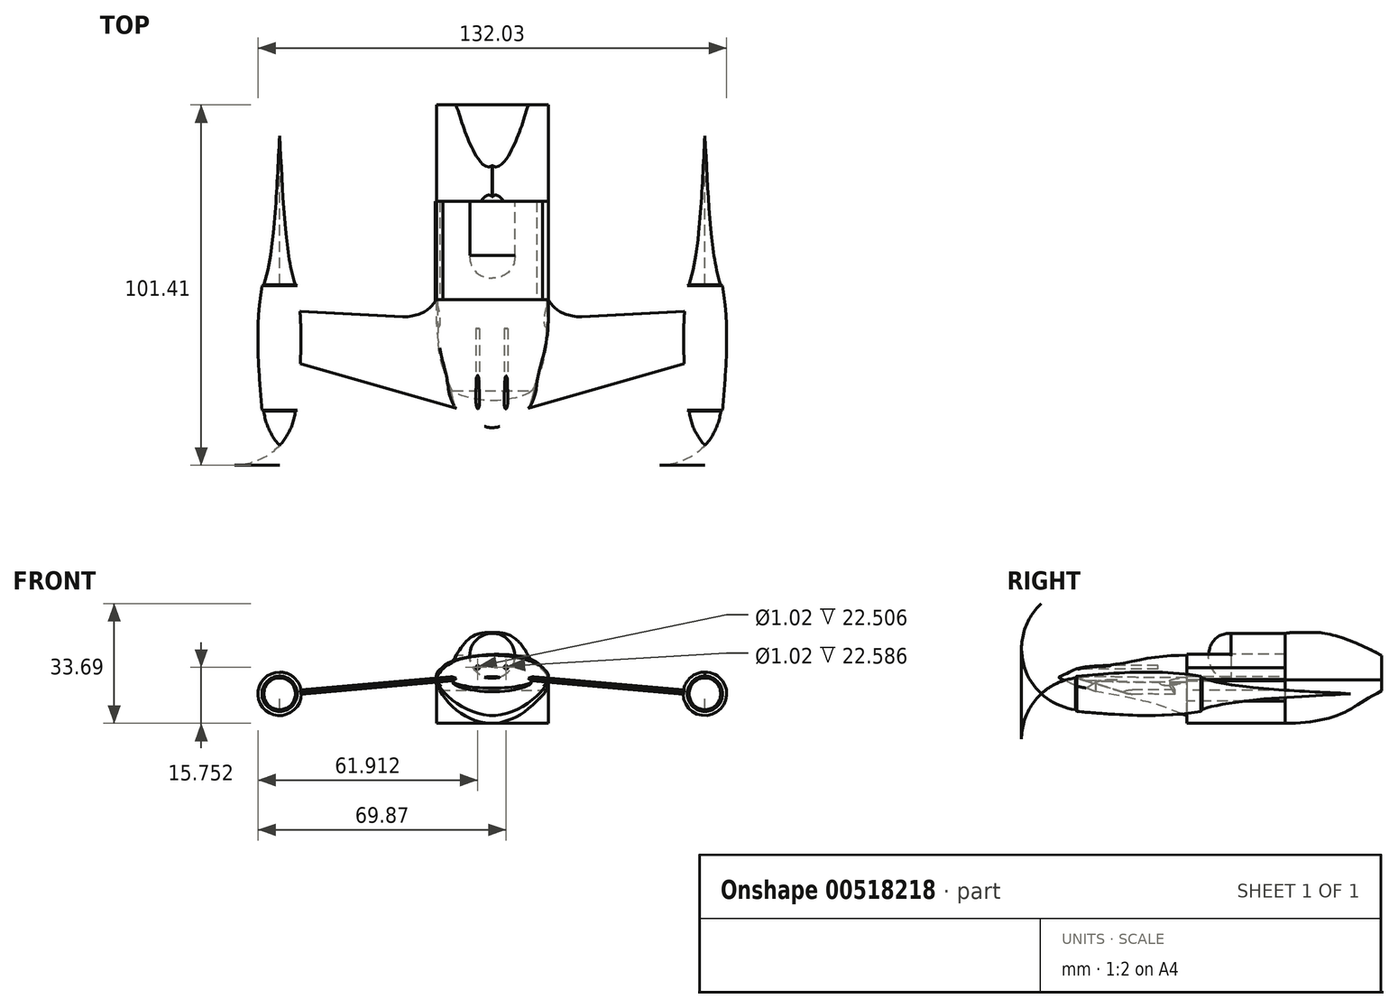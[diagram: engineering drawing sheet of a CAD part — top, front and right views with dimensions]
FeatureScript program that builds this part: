
annotation { "Feature Type Name" : "Feature", "Feature Type Description" : "" }
export const myFeature = defineFeature(function(context is Context, id is Id, definition is map)
    precondition{}
    {
        {
            var Q0;
            Q0=qCreatedBy(makeId("Top.planeOp"),FACE);
            var sketch = newSketch(context, id + "F0", { "sketchPlane" : qUnion([Q0])});
            skLineSegment(sketch, "E0", {"start": v(-12.65, -20.32) * mm, "end": v(-63.92, -5.62) * mm});
            skLineSegment(sketch, "E1", {"start": v(-28.8, 5.88) * mm, "end": v(-63.92, 7.72) * mm});
            skFitSpline(sketch, "E2", {"points": [v(-28.8, 5.88) * mm, v(-18.92, 16.89) * mm], "startDerivative": vector(26.2, 1.25) * mm, "endDerivative": vector(2.67, 12.14) * mm});
            skLineSegment(sketch, "E3", {"start": v(-63.92, 7.72) * mm, "end": v(-63.92, -5.62) * mm});
            skSolve(sketch);
        }
        {
            var Q0;
            Q0=qCreatedBy(makeId("Top.planeOp"),FACE);
            var Q1;
            Q1=sQuery(id+"F0.wireOp",EDGE,"E3");
            cPlane(context, id + "F1", {"entities" : qUnion([Q0, Q1]), "cplaneType" : CPlaneType.LINE_ANGLE, "offset" : 25.4 * mm, "angle" : 185 * degree, "width" : 152.4 * mm, "height" : 152.4 * mm});
        }
        {
            var Q0;
            Q0=qCreatedBy(id+"F1.planeOp",FACE);
            var sketch = newSketch(context, id + "F2", { "sketchPlane" : qUnion([Q0])});
            skLineSegment(sketch, "E4", {"start": v(-63.74, 6.67) * mm, "end": v(-63.74, -6.67) * mm});
            skLineSegment(sketch, "E5", {"start": v(-63.74, 6.67) * mm, "end": v(-28.61, 4.83) * mm});
            skLineSegment(sketch, "E6", {"start": v(-63.74, -6.67) * mm, "end": v(-12.47, -21.37) * mm});
            skFitSpline(sketch, "E7", {"points": [v(-28.61, 4.83) * mm, v(-17.53, 15.9) * mm], "startDerivative": vector(29.82, 1.4) * mm, "endDerivative": vector(2.66, 12.89) * mm});
            skFitSpline(sketch, "E8", {"points": [v(-17.53, 15.9) * mm, v(-12.47, -21.37) * mm], "startDerivative": vector(-1.14, -43.58) * mm, "endDerivative": vector(17.08, -27.32) * mm});
            skSolve(sketch);
        }
        {
            var Q0;
            Q0 = qSketchRegion(id + "F2", true);
            extrude(context, id + "F3", {"entities" : qUnion([Q0]), "endBound" : BoundingType.SYMMETRIC, "depth" : 1.27 * mm, "offsetDistance" : 25.4 * mm});
        }
        {
            var Q0;
            Q0=qCreatedBy(makeId("Right.planeOp"),FACE);
            cPlane(context, id + "F4", {"entities" : qUnion([Q0]), "cplaneType" : CPlaneType.OFFSET, "offset" : 63.75 * mm, "oppositeDirection" : true, "width" : 152.4 * mm, "height" : 152.4 * mm});
        }
        {
            var Q0;
            Q0=qCreatedBy(id+"F4.planeOp",FACE);
            var sketch = newSketch(context, id + "F5", { "sketchPlane" : qUnion([Q0])});
            skArc(sketch, "E9", {"start": v(-31.34, 0) * mm, "mid": v(-26.88, -2.98) * mm, "end": v(-21.72, -4.45) * mm});
            skFitSpline(sketch, "E10", {"points": [v(-21.72, -4.95) * mm, v(13.64, -4.95) * mm], "startDerivative": vector(34.57, -2.86) * mm, "endDerivative": vector(36.11, 6.19) * mm});
            skFitSpline(sketch, "E11", {"points": [v(13.95, -4.43) * mm, v(55.82, 0) * mm], "startDerivative": vector(26.67, 9.84) * mm, "endDerivative": vector(28.85, 1.9) * mm});
            skLineSegment(sketch, "E12", {"start": v(13.95, -4.43) * mm, "end": v(13.64, -4.95) * mm});
            skLineSegment(sketch, "E13", {"start": v(-21.39, -4.98) * mm, "end": v(-21.72, -4.45) * mm});
            skLineSegment(sketch, "E14", {"start": v(55.82, 0) * mm, "end": v(-31.34, 0) * mm});
            skSolve(sketch);
        }
        {
            var Q0;
            Q0 = qSketchRegion(id + "F5", true);
            var Q1;
            Q1=sQuery(id+"F5.wireOp",EDGE,"E14");
            revolve(context, id + "F6", {"operationType" : NewBodyOperationType.ADD, "entities" : qUnion([Q0]), "axis" : qUnion([Q1]), "revolveType" : RevolveType.FULL});
        }
        {
            var Q0;
            Q0=qCreatedBy(makeId("Front.planeOp"),FACE);
            cPlane(context, id + "F7", {"entities" : qUnion([Q0]), "cplaneType" : CPlaneType.OFFSET, "offset" : 21.59 * mm, "width" : 152.4 * mm, "height" : 152.4 * mm});
        }
        {
            var Q0;
            Q0=qCreatedBy(makeId("Front.planeOp"),FACE);
            cPlane(context, id + "F8", {"entities" : qUnion([Q0]), "cplaneType" : CPlaneType.OFFSET, "offset" : 6.35 * mm, "width" : 152.4 * mm, "height" : 152.4 * mm});
        }
        {
            var Q0;
            Q0=qCreatedBy(id+"F7.planeOp",FACE);
            var sketch = newSketch(context, id + "F9", { "sketchPlane" : qUnion([Q0])});
            skEllipse(sketch, "E15", {"center": v(-3.86, 4.62) * mm, "majorRadius": 9.54 * mm, "minorRadius": 2.32 * mm, "majorAxis": v(-1, 0)});
            skSolve(sketch);
        }
        {
            var Q0;
            Q0=qCreatedBy(id+"F8.planeOp",FACE);
            var sketch = newSketch(context, id + "F10", { "sketchPlane" : qUnion([Q0])});
            skPoint(sketch, "E16.0", {"position": v(-3.86, 4.62) * mm});
            skEllipse(sketch, "E17", {"center": v(-3.86, 4.62) * mm, "majorRadius": 14.29 * mm, "minorRadius": 4.37 * mm, "majorAxis": v(-1, 0)});
            skSolve(sketch);
        }
        {
            var Q0;
            Q0=qCreatedBy(makeId("Front.planeOp"),FACE);
            var sketch = newSketch(context, id + "F11", { "sketchPlane" : qUnion([Q0])});
            skPoint(sketch, "E18.0", {"position": v(-3.86, 4.62) * mm});
            skEllipse(sketch, "E19", {"center": v(-3.86, 4.62) * mm, "majorRadius": 15.52 * mm, "minorRadius": 5.58 * mm, "majorAxis": v(-1, 0)});
            skSolve(sketch);
        }
        {
            var Q0;
            Q0=qCreatedBy(makeId("Front.planeOp"),FACE);
            cPlane(context, id + "F12", {"entities" : qUnion([Q0]), "cplaneType" : CPlaneType.OFFSET, "offset" : 15.75 * mm, "oppositeDirection" : true, "width" : 152.4 * mm, "height" : 152.4 * mm});
        }
        {
            var Q0;
            Q0=qCreatedBy(id+"F12.planeOp",FACE);
            var sketch = newSketch(context, id + "F13", { "sketchPlane" : qUnion([Q0])});
            skPoint(sketch, "E20.0", {"position": v(-3.86, 4.62) * mm});
            skEllipse(sketch, "E21", {"center": v(-3.86, 4.62) * mm, "majorRadius": 15.24 * mm, "minorRadius": 6.16 * mm, "majorAxis": v(-1, 0)});
            skSolve(sketch);
        }
        {
            var Q0;
            Q0=qCreatedBy(id+"F7.planeOp",FACE);
            cPlane(context, id + "F14", {"entities" : qUnion([Q0]), "cplaneType" : CPlaneType.OFFSET, "offset" : 5.08 * mm, "width" : 152.4 * mm, "height" : 152.4 * mm});
        }
        {
            var Q0;
            Q0=qCreatedBy(id+"F14.planeOp",FACE);
            var sketch = newSketch(context, id + "F15", { "sketchPlane" : qUnion([Q0])});
            skPoint(sketch, "E22.0", {"position": v(-3.86, 4.62) * mm});
            skEllipse(sketch, "E23", {"center": v(-3.86, 4.62) * mm, "majorRadius": 0.64 * mm, "minorRadius": 0.04 * mm, "majorAxis": v(1, 0)});
            skSolve(sketch);
        }
        {
            var Q0;
            Q0=qCreatedBy(id+"F14.planeOp",FACE);
            cPlane(context, id + "F16", {"entities" : qUnion([Q0]), "cplaneType" : CPlaneType.OFFSET, "offset" : 2.8 * mm, "oppositeDirection" : true, "width" : 152.4 * mm, "height" : 152.4 * mm});
        }
        {
            var Q0;
            Q0=qCreatedBy(id+"F16.planeOp",FACE);
            var sketch = newSketch(context, id + "F17", { "sketchPlane" : qUnion([Q0])});
            skPoint(sketch, "E24.0", {"position": v(-3.86, 4.62) * mm});
            skEllipse(sketch, "E25", {"center": v(-3.86, 4.62) * mm, "majorRadius": 6.39 * mm, "minorRadius": 1.25 * mm, "majorAxis": v(-1, 0)});
            skSolve(sketch);
        }
        {
            var Q0;
            Q0=qCreatedBy(id+"F8.planeOp",FACE);
            cPlane(context, id + "F18", {"entities" : qUnion([Q0]), "cplaneType" : CPlaneType.OFFSET, "offset" : 6.6 * mm, "width" : 152.4 * mm, "height" : 152.4 * mm});
        }
        {
            var Q0;
            Q0=qCreatedBy(id+"F18.planeOp",FACE);
            var sketch = newSketch(context, id + "F19", { "sketchPlane" : qUnion([Q0])});
            skPoint(sketch, "E26.0", {"position": v(-3.86, 4.62) * mm});
            skEllipse(sketch, "E27", {"center": v(-3.86, 4.62) * mm, "majorRadius": 12.73 * mm, "minorRadius": 3.38 * mm, "majorAxis": v(-1, 0)});
            skSolve(sketch);
        }
        {
            var Q1;
            Q1=makeQuery(id+"F13.imprint","IMPRINT",FACE,{"disambiguationData":[TD([[makeQuery(id+"F13.imprint","IMPRINT",EDGE,{"derivedFrom":sQuery(id+"F13.wireOp",EDGE,"E21")}),1.0]])]});
            var Q2;
            Q2=makeQuery(id+"F11.imprint","IMPRINT",FACE,{"disambiguationData":[TD([[makeQuery(id+"F11.imprint","IMPRINT",EDGE,{"derivedFrom":sQuery(id+"F11.wireOp",EDGE,"E19")}),1.0]])]});
            var Q3;
            Q3=makeQuery(id+"F10.imprint","IMPRINT",FACE,{"disambiguationData":[TD([[makeQuery(id+"F10.imprint","IMPRINT",EDGE,{"derivedFrom":sQuery(id+"F10.wireOp",EDGE,"E17")}),1.0]])]});
            var Q4;
            Q4=makeQuery(id+"F19.imprint","IMPRINT",FACE,{"disambiguationData":[TD([[makeQuery(id+"F19.imprint","IMPRINT",EDGE,{"derivedFrom":sQuery(id+"F19.wireOp",EDGE,"E27")}),1.0]])]});
            var Q5;
            Q5=makeQuery(id+"F9.imprint","IMPRINT",FACE,{"disambiguationData":[TD([[makeQuery(id+"F9.imprint","IMPRINT",EDGE,{"derivedFrom":sQuery(id+"F9.wireOp",EDGE,"E15")}),1.0]])]});
            var Q6;
            Q6=makeQuery(id+"F17.imprint","IMPRINT",FACE,{"disambiguationData":[TD([[makeQuery(id+"F17.imprint","IMPRINT",EDGE,{"derivedFrom":sQuery(id+"F17.wireOp",EDGE,"E25")}),1.0]])]});
            var Q7;
            Q7=makeQuery(id+"F15.imprint","IMPRINT",FACE,{"disambiguationData":[TD([[makeQuery(id+"F15.imprint","IMPRINT",EDGE,{"derivedFrom":sQuery(id+"F15.wireOp",EDGE,"E23")}),1.0]])]});
            loft(context, id + "F20", {"operationType" : NewBodyOperationType.ADD, "sheetProfilesArray" : [{ "sheetProfileEntities" : qUnion([Q1]) }, { "sheetProfileEntities" : qUnion([Q2]) }, { "sheetProfileEntities" : qUnion([Q3]) }, { "sheetProfileEntities" : qUnion([Q4]) }, { "sheetProfileEntities" : qUnion([Q5]) }, { "sheetProfileEntities" : qUnion([Q6]) }, { "sheetProfileEntities" : qUnion([Q7]) }]});
        }
        {
            var Q0;
            Q0=qCreatedBy(makeId("Top.planeOp"),FACE);
            var sketch = newSketch(context, id + "F21", { "sketchPlane" : qUnion([Q0])});
            skArc(sketch, "E28", {"start": v(-6.4, -25.84) * mm, "mid": v(-3.86, -26.34) * mm, "end": v(-1.32, -25.84) * mm});
            skFitSpline(sketch, "E29.0", {"points": [v(-4.5, -26.67) * mm, v(-4.07, -26.67) * mm, v(-3.64, -26.67) * mm, v(-3.22, -26.67) * mm]});
            skLineSegment(sketch, "E30", {"start": v(-6.4, -25.84) * mm, "end": v(-3.91, -27.54) * mm});
            skLineSegment(sketch, "E31", {"start": v(-3.91, -27.54) * mm, "end": v(-1.32, -25.84) * mm});
            skSolve(sketch);
        }
        {
            var Q0;
            Q0 = qSketchRegion(id + "F21", true);
            extrude(context, id + "F22", {"entities" : qUnion([Q0]), "operationType" : NewBodyOperationType.REMOVE, "endBound" : BoundingType.THROUGH_ALL, "depth" : 25.4 * mm, "offsetDistance" : 25.4 * mm});
        }
        {
            var Q0;
            Q0=qCreatedBy(makeId("Right.planeOp"),FACE);
            cPlane(context, id + "F23", {"entities" : qUnion([Q0]), "cplaneType" : CPlaneType.OFFSET, "offset" : 3.86 * mm, "oppositeDirection" : true, "width" : 152.4 * mm, "height" : 152.4 * mm});
        }
        {
            var Q0;
            Q0=makeQuery(id+"F3.opExtrude","SWEPT_BODY",BODY,{"disambiguationData":[OSD([sQuery(id+"F2.wireOp",EDGE,"E4"),sQuery(id+"F2.wireOp",EDGE,"E5"),sQuery(id+"F2.wireOp",EDGE,"E6"),sQuery(id+"F2.wireOp",EDGE,"E7"),sQuery(id+"F2.wireOp",EDGE,"E8")])]});
            var Q1;
            Q1=qCreatedBy(id+"F23.planeOp",FACE);
            mirror(context, id + "F24", {"operationType" : NewBodyOperationType.ADD, "entities" : qUnion([Q0]), "mirrorPlane" : qUnion([Q1])});
        }
        {
            var Q0;
            Q0=qCreatedBy(id+"F16.planeOp",FACE);
            var sketch = newSketch(context, id + "F25", { "sketchPlane" : qUnion([Q0])});
            skCircle(sketch, "E32", {"center": v(0, 7.44) * mm, "radius": 0.5 * mm});
            skCircle(sketch, "E33", {"center": v(-7.96, 7.44) * mm, "radius": 0.5 * mm});
            skSolve(sketch);
        }
        {
            var Q0;
            Q0 = qSketchRegion(id + "F25", true);
            extrude(context, id + "F26", {"entities" : qUnion([Q0]), "operationType" : NewBodyOperationType.REMOVE, "oppositeDirection" : true, "depth" : 25.4 * mm, "offsetDistance" : 25.4 * mm});
        }
        {
            var Q0;
            Q0=makeQuery(id+"F3.opExtrude","CAP_EDGE",EDGE,{"disambiguationData":[OSD([sQuery(id+"F2.wireOp",EDGE,"E6")])],"isStart":false});
            var Q1;
            Q1=makeQuery(id+"F3.opExtrude","CAP_EDGE",EDGE,{"disambiguationData":[OSD([sQuery(id+"F2.wireOp",EDGE,"E6")])],"isStart":true});
            var Q2;
            Q2=makeQuery(id+"F24.opPattern","COPY",EDGE,{"derivedFrom":makeQuery(id+"F3.opExtrude","CAP_EDGE",EDGE,{"disambiguationData":[OSD([sQuery(id+"F2.wireOp",EDGE,"E6")])],"isStart":false}),"instanceName":"1"});
            var Q3;
            Q3=makeQuery(id+"F24.opPattern","COPY",EDGE,{"derivedFrom":makeQuery(id+"F3.opExtrude","CAP_EDGE",EDGE,{"disambiguationData":[OSD([sQuery(id+"F2.wireOp",EDGE,"E6")])],"isStart":true}),"instanceName":"1"});
            chamfer(context, id + "F27", {"entities" : qUnion([Q0, Q1, Q2, Q3]), "width" : 0.76 * mm, "tangentPropagation" : true});
        }
        {
            var Q0;
            Q0=makeQuery(id+"F13.imprint","IMPRINT",FACE,{"disambiguationData":[TD([[makeQuery(id+"F13.imprint","IMPRINT",EDGE,{"derivedFrom":sQuery(id+"F13.wireOp",EDGE,"E21")}),1.0]])]});
            cPlane(context, id + "F28", {"entities" : qUnion([Q0]), "cplaneType" : CPlaneType.OFFSET, "offset" : 6.35 * mm, "oppositeDirection" : true, "width" : 152.4 * mm, "height" : 152.4 * mm});
        }
        {
            var Q0;
            Q0=qCreatedBy(id+"F28.planeOp",FACE);
            cPlane(context, id + "F29", {"entities" : qUnion([Q0]), "cplaneType" : CPlaneType.OFFSET, "offset" : 6.35 * mm, "oppositeDirection" : true, "width" : 152.4 * mm, "height" : 152.4 * mm});
        }
        {
            var Q0;
            Q0=qCreatedBy(id+"F29.planeOp",FACE);
            cPlane(context, id + "F30", {"entities" : qUnion([Q0]), "cplaneType" : CPlaneType.OFFSET, "offset" : 6.35 * mm, "oppositeDirection" : true, "width" : 152.4 * mm, "height" : 152.4 * mm});
        }
        {
            var Q0;
            Q0=qCreatedBy(id+"F30.planeOp",FACE);
            cPlane(context, id + "F31", {"entities" : qUnion([Q0]), "cplaneType" : CPlaneType.OFFSET, "offset" : 6.35 * mm, "oppositeDirection" : true, "width" : 152.4 * mm, "height" : 152.4 * mm});
        }
        {
            var Q0;
            Q0=qCreatedBy(id+"F31.planeOp",FACE);
            cPlane(context, id + "F32", {"entities" : qUnion([Q0]), "cplaneType" : CPlaneType.OFFSET, "offset" : 6.35 * mm, "oppositeDirection" : true, "width" : 152.4 * mm, "height" : 152.4 * mm});
        }
        {
            var Q0;
            Q0=qCreatedBy(id+"F32.planeOp",FACE);
            cPlane(context, id + "F33", {"entities" : qUnion([Q0]), "cplaneType" : CPlaneType.OFFSET, "offset" : 6.35 * mm, "oppositeDirection" : true, "width" : 152.4 * mm, "height" : 152.4 * mm});
        }
        {
            var Q0;
            Q0=qCreatedBy(id+"F33.planeOp",FACE);
            cPlane(context, id + "F34", {"entities" : qUnion([Q0]), "cplaneType" : CPlaneType.OFFSET, "offset" : 6.35 * mm, "oppositeDirection" : true, "width" : 152.4 * mm, "height" : 152.4 * mm});
        }
        {
            var Q0;
            Q0=qCreatedBy(id+"F34.planeOp",FACE);
            cPlane(context, id + "F35", {"entities" : qUnion([Q0]), "cplaneType" : CPlaneType.OFFSET, "offset" : 6.35 * mm, "oppositeDirection" : true, "width" : 152.4 * mm, "height" : 152.4 * mm});
        }
        {
            var Q0;
            Q0=qCreatedBy(id+"F35.planeOp",FACE);
            cPlane(context, id + "F36", {"entities" : qUnion([Q0]), "cplaneType" : CPlaneType.OFFSET, "offset" : 6.35 * mm, "oppositeDirection" : true, "width" : 152.4 * mm, "height" : 152.4 * mm});
        }
        {
            var Q0;
            Q0=qCreatedBy(id+"F36.planeOp",FACE);
            cPlane(context, id + "F37", {"entities" : qUnion([Q0]), "cplaneType" : CPlaneType.OFFSET, "offset" : 6.35 * mm, "oppositeDirection" : true, "width" : 152.4 * mm, "height" : 152.4 * mm});
        }
        {
            var Q0;
            Q0=qCreatedBy(id+"F37.planeOp",FACE);
            cPlane(context, id + "F38", {"entities" : qUnion([Q0]), "cplaneType" : CPlaneType.OFFSET, "offset" : 6.35 * mm, "oppositeDirection" : true, "width" : 152.4 * mm, "height" : 152.4 * mm});
        }
        {
            var Q0;
            Q0=qCreatedBy(id+"F38.planeOp",FACE);
            cPlane(context, id + "F39", {"entities" : qUnion([Q0]), "cplaneType" : CPlaneType.OFFSET, "offset" : 6.35 * mm, "oppositeDirection" : true, "width" : 152.4 * mm, "height" : 152.4 * mm});
        }
        {
            var Q0;
            Q0=qCreatedBy(id+"F39.planeOp",FACE);
            cPlane(context, id + "F40", {"entities" : qUnion([Q0]), "cplaneType" : CPlaneType.OFFSET, "offset" : 6.35 * mm, "oppositeDirection" : true, "width" : 152.4 * mm, "height" : 152.4 * mm});
        }
        {
            var Q0;
            Q0=qCreatedBy(id+"F40.planeOp",FACE);
            cPlane(context, id + "F41", {"entities" : qUnion([Q0]), "cplaneType" : CPlaneType.OFFSET, "offset" : 6.35 * mm, "oppositeDirection" : true, "width" : 152.4 * mm, "height" : 152.4 * mm});
        }
        {
            var Q0;
            {var subQ0=sQuery(id+"F2.wireOp",EDGE,"E7");var subQ1=sQuery(id+"F2.wireOp",EDGE,"E6");var subQ2=sQuery(id+"F2.wireOp",EDGE,"E5");Q0=makeQuery(id+"F27.opChamfer","BLEND_EDGE",EDGE,{"blendedFrom":[makeQuery(id+"F24.opPattern","COPY",EDGE,{"derivedFrom":makeQuery(id+"F3.opExtrude","CAP_EDGE",EDGE,{"disambiguationData":[OSD([subQ1])],"isStart":false}),"instanceName":"1"}),makeQuery(id+"F24.opPattern","COPY",FACE,{"derivedFrom":makeQuery(id+"F20.boolean.opBoolean","SPLIT",FACE,{"disambiguationData":[TD([makeQuery(id+"F3.opExtrude","SWEPT_FACE",FACE,{"disambiguationData":[OSD([subQ2])]})])],"derivedFrom":makeQuery(id+"F3.opExtrude","CAP_FACE",FACE,{"disambiguationData":[OSD([sQuery(id+"F2.wireOp",EDGE,"E4"),subQ2,subQ1,subQ0,sQuery(id+"F2.wireOp",EDGE,"E8")])],"isStart":false})}),"instanceName":"1"})],"blendedInto":[makeQuery(id+"F24.opPattern","COPY",FACE,{"derivedFrom":makeQuery(id+"F20.boolean.opBoolean","SPLIT",FACE,{"disambiguationData":[TD([makeQuery(id+"F3.opExtrude","SWEPT_FACE",FACE,{"disambiguationData":[OSD([subQ2])]})])],"derivedFrom":makeQuery(id+"F3.opExtrude","CAP_FACE",FACE,{"disambiguationData":[OSD([sQuery(id+"F2.wireOp",EDGE,"E4"),subQ2,subQ1,subQ0,sQuery(id+"F2.wireOp",EDGE,"E8")])],"isStart":false})}),"instanceName":"1"})]});}
            var Q1;
            {var subQ0=sQuery(id+"F2.wireOp",EDGE,"E8");var subQ1=sQuery(id+"F2.wireOp",EDGE,"E7");var subQ2=sQuery(id+"F2.wireOp",EDGE,"E6");var subQ3=sQuery(id+"F2.wireOp",EDGE,"E5");Q1=makeQuery(id+"F27.opChamfer","BLEND_EDGE",EDGE,{"blendedFrom":[makeQuery(id+"F24.opPattern","COPY",EDGE,{"derivedFrom":makeQuery(id+"F3.opExtrude","CAP_EDGE",EDGE,{"disambiguationData":[OSD([subQ2])],"isStart":true}),"instanceName":"1"}),makeQuery(id+"F24.opPattern","COPY",FACE,{"derivedFrom":makeQuery(id+"F20.boolean.opBoolean","SPLIT",FACE,{"disambiguationData":[TD([makeQuery(id+"F3.opExtrude","SWEPT_FACE",FACE,{"disambiguationData":[OSD([subQ3])]})])],"derivedFrom":makeQuery(id+"F3.opExtrude","CAP_FACE",FACE,{"disambiguationData":[OSD([sQuery(id+"F2.wireOp",EDGE,"E4"),subQ3,subQ2,subQ1,subQ0])],"isStart":true})}),"instanceName":"1"})],"blendedInto":[makeQuery(id+"F24.opPattern","COPY",FACE,{"derivedFrom":makeQuery(id+"F20.boolean.opBoolean","SPLIT",FACE,{"disambiguationData":[TD([makeQuery(id+"F3.opExtrude","SWEPT_FACE",FACE,{"disambiguationData":[OSD([subQ3])]})])],"derivedFrom":makeQuery(id+"F3.opExtrude","CAP_FACE",FACE,{"disambiguationData":[OSD([sQuery(id+"F2.wireOp",EDGE,"E4"),subQ3,subQ2,subQ1,subQ0])],"isStart":true})}),"instanceName":"1"})]});}
            var Q2;
            {var subQ0=sQuery(id+"F2.wireOp",EDGE,"E7");var subQ1=sQuery(id+"F2.wireOp",EDGE,"E6");var subQ2=sQuery(id+"F2.wireOp",EDGE,"E5");Q2=makeQuery(id+"F27.opChamfer","BLEND_EDGE",EDGE,{"blendedFrom":[makeQuery(id+"F3.opExtrude","CAP_EDGE",EDGE,{"disambiguationData":[OSD([subQ1])],"isStart":false}),makeQuery(id+"F20.boolean.opBoolean","SPLIT",FACE,{"disambiguationData":[TD([makeQuery(id+"F3.opExtrude","SWEPT_FACE",FACE,{"disambiguationData":[OSD([subQ2])]})])],"derivedFrom":makeQuery(id+"F3.opExtrude","CAP_FACE",FACE,{"disambiguationData":[OSD([sQuery(id+"F2.wireOp",EDGE,"E4"),subQ2,subQ1,subQ0,sQuery(id+"F2.wireOp",EDGE,"E8")])],"isStart":false})})],"blendedInto":[makeQuery(id+"F20.boolean.opBoolean","SPLIT",FACE,{"disambiguationData":[TD([makeQuery(id+"F3.opExtrude","SWEPT_FACE",FACE,{"disambiguationData":[OSD([subQ2])]})])],"derivedFrom":makeQuery(id+"F3.opExtrude","CAP_FACE",FACE,{"disambiguationData":[OSD([sQuery(id+"F2.wireOp",EDGE,"E4"),subQ2,subQ1,subQ0,sQuery(id+"F2.wireOp",EDGE,"E8")])],"isStart":false})})]});}
            var Q3;
            {var subQ0=sQuery(id+"F2.wireOp",EDGE,"E8");var subQ1=sQuery(id+"F2.wireOp",EDGE,"E7");var subQ2=sQuery(id+"F2.wireOp",EDGE,"E6");var subQ3=sQuery(id+"F2.wireOp",EDGE,"E5");Q3=makeQuery(id+"F27.opChamfer","BLEND_EDGE",EDGE,{"blendedFrom":[makeQuery(id+"F3.opExtrude","CAP_EDGE",EDGE,{"disambiguationData":[OSD([subQ2])],"isStart":true}),makeQuery(id+"F20.boolean.opBoolean","SPLIT",FACE,{"disambiguationData":[TD([makeQuery(id+"F3.opExtrude","SWEPT_FACE",FACE,{"disambiguationData":[OSD([subQ3])]})])],"derivedFrom":makeQuery(id+"F3.opExtrude","CAP_FACE",FACE,{"disambiguationData":[OSD([sQuery(id+"F2.wireOp",EDGE,"E4"),subQ3,subQ2,subQ1,subQ0])],"isStart":true})})],"blendedInto":[makeQuery(id+"F20.boolean.opBoolean","SPLIT",FACE,{"disambiguationData":[TD([makeQuery(id+"F3.opExtrude","SWEPT_FACE",FACE,{"disambiguationData":[OSD([subQ3])]})])],"derivedFrom":makeQuery(id+"F3.opExtrude","CAP_FACE",FACE,{"disambiguationData":[OSD([sQuery(id+"F2.wireOp",EDGE,"E4"),subQ3,subQ2,subQ1,subQ0])],"isStart":true})})]});}
            fillet(context, id + "F42", {"entities" : qUnion([Q0, Q1, Q2, Q3]), "radius" : 5.08 * mm, "tangentPropagation" : true, "allowEdgeOverflow" : false});
        }
        {
            var Q0;
            Q0=qCreatedBy(id+"F28.planeOp",FACE);
            cPlane(context, id + "F43", {"entities" : qUnion([Q0]), "cplaneType" : CPlaneType.OFFSET, "offset" : 6.35 * mm, "width" : 152.4 * mm, "height" : 152.4 * mm});
        }
        {
            var Q0;
            Q0=qCreatedBy(id+"F43.planeOp",FACE);
            cPlane(context, id + "F44", {"entities" : qUnion([Q0]), "cplaneType" : CPlaneType.OFFSET, "offset" : 6.35 * mm, "width" : 152.4 * mm, "height" : 152.4 * mm});
        }
        {
            var Q0;
            Q0=qCreatedBy(id+"F44.planeOp",FACE);
            cPlane(context, id + "F45", {"entities" : qUnion([Q0]), "cplaneType" : CPlaneType.OFFSET, "offset" : 6.35 * mm, "width" : 152.4 * mm, "height" : 152.4 * mm});
        }
        {
            var Q0;
            Q0=qCreatedBy(id+"F45.planeOp",FACE);
            cPlane(context, id + "F46", {"entities" : qUnion([Q0]), "cplaneType" : CPlaneType.OFFSET, "offset" : 6.35 * mm, "width" : 152.4 * mm, "height" : 152.4 * mm});
        }
        {
            var Q0;
            Q0=qCreatedBy(id+"F46.planeOp",FACE);
            var sketch = newSketch(context, id + "F47", { "sketchPlane" : qUnion([Q0])});
            skFitSpline(sketch, "E34", {"points": [v(-19.58, 3.93) * mm, v(-14.39, 0) * mm, v(-3.8, -1.84) * mm, v(6.67, 0) * mm, v(11.87, 3.88) * mm], "startDerivative": vector(14.64, -24.75) * mm, "endDerivative": vector(15.16, 24.08) * mm});
            skLineSegment(sketch, "E35", {"start": v(-19.58, 3.93) * mm, "end": v(11.87, 3.88) * mm});
            skSolve(sketch);
        }
        {
            var Q0;
            Q0=qCreatedBy(id+"F45.planeOp",FACE);
            var sketch = newSketch(context, id + "F48", { "sketchPlane" : qUnion([Q0])});
            skLineSegment(sketch, "E36.0", {"start": v(-19.58, 3.93) * mm, "end": v(11.87, 3.88) * mm});
            skFitSpline(sketch, "E37", {"points": [v(-19.58, 3.93) * mm, v(-16.04, 0) * mm, v(-3.8, -3.61) * mm, v(8.33, 0) * mm, v(11.87, 3.88) * mm], "startDerivative": vector(14.16, -20.4) * mm, "endDerivative": vector(15.04, 19.9) * mm});
            skPoint(sketch, "E38.0", {"position": v(-14.39, 0) * mm});
            skPoint(sketch, "E39.0", {"position": v(6.67, 0) * mm});
            skSolve(sketch);
        }
        {
            var Q0;
            Q0=qCreatedBy(id+"F44.planeOp",FACE);
            var sketch = newSketch(context, id + "F49", { "sketchPlane" : qUnion([Q0])});
            skLineSegment(sketch, "E40.0", {"start": v(-19.58, 3.93) * mm, "end": v(11.87, 3.88) * mm});
            skPoint(sketch, "E41.0", {"position": v(-3.8, -3.61) * mm});
            skPoint(sketch, "E42.0", {"position": v(8.33, 0) * mm});
            skPoint(sketch, "E43.0", {"position": v(-16.04, 0) * mm});
            skFitSpline(sketch, "E44", {"points": [v(-19.58, 3.93) * mm, v(-17.05, 0) * mm, v(-3.8, -6.08) * mm, v(9.34, 0) * mm, v(11.87, 3.88) * mm], "startDerivative": vector(9, -20.7) * mm, "endDerivative": vector(8.66, 20.62) * mm});
            skSolve(sketch);
        }
        {
            var Q0;
            Q0=qCreatedBy(id+"F43.planeOp",FACE);
            var sketch = newSketch(context, id + "F50", { "sketchPlane" : qUnion([Q0])});
            skLineSegment(sketch, "E45.0", {"start": v(-19.58, 3.93) * mm, "end": v(11.87, 3.88) * mm});
            skPoint(sketch, "E46.0", {"position": v(-3.8, -6.08) * mm});
            skFitSpline(sketch, "E47", {"points": [v(-19.58, 3.93) * mm, v(-17.82, 0) * mm, v(-3.8, -7.6) * mm, v(10.1, 0) * mm, v(11.87, 3.88) * mm], "startDerivative": vector(0, -6.55) * mm, "endDerivative": vector(-1.42, 12.51) * mm});
            skPoint(sketch, "E48.0", {"position": v(-17.05, 0) * mm});
            skPoint(sketch, "E49.0", {"position": v(9.34, 0) * mm});
            skSolve(sketch);
        }
        {
            var Q0;
            Q0=qCreatedBy(id+"F28.planeOp",FACE);
            cPlane(context, id + "F51", {"entities" : qUnion([Q0]), "cplaneType" : CPlaneType.OFFSET, "offset" : 38.1 * mm, "width" : 152.4 * mm, "height" : 152.4 * mm});
        }
        {
            var Q0;
            Q0=qCreatedBy(id+"F51.planeOp",FACE);
            var sketch = newSketch(context, id + "F52", { "sketchPlane" : qUnion([Q0])});
            skLineSegment(sketch, "E50.0", {"start": v(-19.58, 3.93) * mm, "end": v(11.87, 3.88) * mm});
            skPoint(sketch, "E51.2.internal.snap0", {"position": v(-3.85, 3.9) * mm});
            skFitSpline(sketch, "E51", {"points": [v(-15.36, 3.92) * mm, v(-14.27, 2.5) * mm, v(-3.85, 0.6) * mm, v(6.56, 2.5) * mm, v(7.57, 3.89) * mm], "startDerivative": vector(4.7, -10.2) * mm, "endDerivative": vector(4.41, 10.18) * mm});
            skSolve(sketch);
        }
        {
            var Q1;
            Q1 = qSketchRegion(id + "F52", true);
            var Q2;
            Q2 = qSketchRegion(id + "F47", true);
            var Q3;
            Q3 = qSketchRegion(id + "F48", true);
            var Q4;
            Q4 = qSketchRegion(id + "F49", true);
            var Q5;
            Q5 = qSketchRegion(id + "F50", true);
            loft(context, id + "F53", {"operationType" : NewBodyOperationType.ADD, "sheetProfilesArray" : [{ "sheetProfileEntities" : qUnion([Q1]) }, { "sheetProfileEntities" : qUnion([Q2]) }, { "sheetProfileEntities" : qUnion([Q3]) }, { "sheetProfileEntities" : qUnion([Q4]) }, { "sheetProfileEntities" : qUnion([Q5]) }]});
        }
        {
            var Q1;
            Q1 = qSketchRegion(id + "F52", true);
            var Q2;
            Q2=makeQuery(id+"F22.boolean.opBoolean","COPY",FACE,{"derivedFrom":makeQuery(id+"F22.opExtrude","SWEPT_FACE",FACE,{"disambiguationData":[OSD([sQuery(id+"F21.wireOp",EDGE,"E28")])]})});
            loft(context, id + "F54", {"operationType" : NewBodyOperationType.ADD, "sheetProfilesArray" : [{ "sheetProfileEntities" : qUnion([Q1]) }, { "sheetProfileEntities" : qUnion([Q2]) }]});
        }
        {
            var Q0;
            Q0=qCreatedBy(id+"F28.planeOp",FACE);
            var sketch = newSketch(context, id + "F55", { "sketchPlane" : qUnion([Q0])});
            skPoint(sketch, "E52.0", {"position": v(11.87, 3.88) * mm});
            skPoint(sketch, "E53.0", {"position": v(-19.58, 3.93) * mm});
            skFitSpline(sketch, "E54", {"points": [v(11.87, 3.88) * mm, v(11.28, 5.54) * mm, v(8.29, 8.3) * mm, v(-0.9, 10.75) * mm, v(-6.91, 10.72) * mm, v(-13.13, 9.54) * mm, v(-17.35, 7.57) * mm, v(-19.03, 5.54) * mm, v(-19.58, 3.93) * mm, v(-18.2, 0.62) * mm, v(-15.3, -3.03) * mm, v(-11.32, -5.85) * mm, v(-6.7, -7.57) * mm, v(-2.28, -7.76) * mm, v(0.86, -6.95) * mm, v(4.05, -5.34) * mm, v(8.02, -2.4) * mm, v(11.15, 1.32) * mm, v(11.87, 3.88) * mm]});
            skLineSegment(sketch, "E55", {"start": v(1.45, 10.41) * mm, "end": v(-9.17, 10.41) * mm});
            skPoint(sketch, "E56.0", {"position": v(-3.86, 4.62) * mm});
            skSolve(sketch);
        }
        {
            var Q0;
            Q0=qCreatedBy(id+"F29.planeOp",FACE);
            var sketch = newSketch(context, id + "F56", { "sketchPlane" : qUnion([Q0])});
            skPoint(sketch, "E57.0", {"position": v(11.87, 3.88) * mm});
            skPoint(sketch, "E58.0", {"position": v(-19.58, 3.93) * mm});
            skPoint(sketch, "E59.0", {"position": v(1.45, 10.41) * mm});
            skPoint(sketch, "E60.0", {"position": v(-9.17, 10.41) * mm});
            skPoint(sketch, "E61.0", {"position": v(11.28, 5.54) * mm});
            skPoint(sketch, "E62.0", {"position": v(8.29, 8.3) * mm});
            skPoint(sketch, "E63.0", {"position": v(-0.9, 10.75) * mm});
            skPoint(sketch, "E64.0", {"position": v(-6.91, 10.72) * mm});
            skPoint(sketch, "E65.0", {"position": v(-13.13, 9.54) * mm});
            skPoint(sketch, "E66.0", {"position": v(-17.35, 7.57) * mm});
            skPoint(sketch, "E67.0", {"position": v(-19.03, 5.54) * mm});
            skFitSpline(sketch, "E68", {"points": [v(11.87, 3.88) * mm, v(11.28, 5.54) * mm, v(8.29, 8.3) * mm, v(1.45, 10.41) * mm, v(-0.9, 10.75) * mm, v(-6.91, 10.72) * mm, v(-9.17, 10.41) * mm, v(-13.13, 9.54) * mm, v(-17.35, 7.57) * mm, v(-19.03, 5.54) * mm, v(-19.58, 3.93) * mm, v(-18.36, 0.5) * mm, v(-15.46, -3.24) * mm, v(-11.52, -6.2) * mm, v(-6.91, -8) * mm, v(-2.26, -8.2) * mm, v(0.98, -7.33) * mm, v(4.2, -5.76) * mm, v(8.1, -2.62) * mm, v(11.28, 1.12) * mm, v(11.87, 3.88) * mm]});
            skLineSegment(sketch, "E69", {"start": v(1.45, 10.41) * mm, "end": v(-9.17, 10.41) * mm});
            skSolve(sketch);
        }
        {
            var Q0;
            Q0=qCreatedBy(id+"F30.planeOp",FACE);
            var sketch = newSketch(context, id + "F57", { "sketchPlane" : qUnion([Q0])});
            skFitSpline(sketch, "E70.0.0", {"points": [v(11.87, 3.88) * mm, v(11.85, 4.48) * mm, v(11.32, 5.71) * mm, v(8.47, 9.06) * mm, v(-1.07, 11.1) * mm, v(-6.73, 10.87) * mm, v(-13.08, 9.78) * mm, v(-17.45, 7.93) * mm, v(-19.04, 5.6) * mm, v(-19.97, 3.87) * mm, v(-18.21, 0.38) * mm, v(-15.47, -3.22) * mm, v(-11.4, -6.02) * mm, v(-6.82, -7.82) * mm, v(-2.29, -7.95) * mm, v(0.91, -7.04) * mm, v(4.17, -5.39) * mm, v(8.1, -2.57) * mm, v(11.33, 1.03) * mm, v(11.9, 3.14) * mm, v(11.87, 3.88) * mm]});
            skLineSegment(sketch, "E70.0.1", {"start": v(1.45, 10.41) * mm, "end": v(-9.17, 10.41) * mm});
            skSolve(sketch);
        }
        {
            var Q0;
            Q0=qCreatedBy(id+"F28.planeOp",FACE);
            cPlane(context, id + "F58", {"entities" : qUnion([Q0]), "cplaneType" : CPlaneType.OFFSET, "offset" : 12.45 * mm, "width" : 152.4 * mm, "height" : 152.4 * mm});
        }
        {
            var Q0;
            Q0=qCreatedBy(id+"F58.planeOp",FACE);
            var sketch = newSketch(context, id + "F59", { "sketchPlane" : qUnion([Q0])});
            skPoint(sketch, "E71.0", {"position": v(-3.86, 4.62) * mm});
            skLineSegment(sketch, "E72", {"start": v(-3.86, 7) * mm, "end": v(-3.86, 2.15) * mm});
            skSolve(sketch);
        }
        {
            var Q0;
            Q0 = qBodyType(qCreatedBy(id + "F59" ,EDGE), BodyType.WIRE);
            var Q1;
            Q1=qCreatedBy(id+"F58.planeOp",FACE);
            cPlane(context, id + "F60", {"entities" : qUnion([Q0, Q1]), "cplaneType" : CPlaneType.LINE_ANGLE, "offset" : 25.4 * mm, "angle" : 90 * degree, "width" : 152.4 * mm, "height" : 152.4 * mm});
        }
        {
            var Q0;
            Q0=qCreatedBy(id+"F60.planeOp",FACE);
            var sketch = newSketch(context, id + "F61", { "sketchPlane" : qUnion([Q0])});
            skLineSegment(sketch, "E73.bottom", {"start": v(9.65, 12.39) * mm, "end": v(18.37, 12.39) * mm});
            skLineSegment(sketch, "E73.top", {"start": v(9.65, -13.23) * mm, "end": v(18.37, -13.23) * mm});
            skLineSegment(sketch, "E73.left", {"start": v(9.65, 12.39) * mm, "end": v(9.65, -13.23) * mm});
            skLineSegment(sketch, "E73.right", {"start": v(18.37, 12.39) * mm, "end": v(18.37, -13.23) * mm});
            skSolve(sketch);
        }
        {
            var Q0;
            Q0 = qSketchRegion(id + "F61", true);
            extrude(context, id + "F62", {"entities" : qUnion([Q0]), "operationType" : NewBodyOperationType.REMOVE, "endBound" : BoundingType.SYMMETRIC, "oppositeDirection" : true, "depth" : 50.8 * mm, "offsetDistance" : 25.4 * mm});
        }
        {
            var Q0;
            Q0=makeQuery(id+"F62.boolean.opBoolean","COPY",FACE,{"derivedFrom":makeQuery(id+"F62.opExtrude","SWEPT_FACE",FACE,{"disambiguationData":[OSD([sQuery(id+"F61.wireOp",EDGE,"E73.left")])]})});
            var sketch = newSketch(context, id + "F63", { "sketchPlane" : qUnion([Q0])});
            skFitSpline(sketch, "E74.0", {"points": [v(19.56, 4.62) * mm, v(19.56, 5.44) * mm, v(19.15, 6.25) * mm, v(17.58, 7.76) * mm, v(16.41, 8.45) * mm, v(13.5, 9.6) * mm, v(11.76, 10.06) * mm, v(7.97, 10.68) * mm, v(5.91, 10.85) * mm, v(1.8, 10.85) * mm, v(-0.25, 10.68) * mm, v(-4.05, 10.06) * mm, v(-5.8, 9.6) * mm, v(-8.7, 8.45) * mm, v(-9.86, 7.76) * mm, v(-11.44, 6.25) * mm, v(-11.84, 5.44) * mm, v(-11.84, 3.8) * mm, v(-11.44, 3) * mm, v(-9.86, 1.49) * mm, v(-8.7, 0.8) * mm, v(-5.8, -0.36) * mm, v(-4.05, -0.82) * mm, v(-0.25, -1.44) * mm, v(1.8, -1.6) * mm, v(5.91, -1.6) * mm, v(7.97, -1.44) * mm, v(11.76, -0.82) * mm, v(13.5, -0.36) * mm, v(16.41, 0.8) * mm, v(17.58, 1.49) * mm, v(19.15, 3) * mm, v(19.56, 3.8) * mm, v(19.56, 4.62) * mm]});
            skFitSpline(sketch, "E75.0", {"points": [v(-11.87, 3.88) * mm, v(-11.53, 3.02) * mm, v(-11.15, 2.2) * mm, v(-10.3, 1.04) * mm, v(-10.1, 0.8) * mm, v(-9.68, 0.32) * mm, v(-9.45, 0.07) * mm, v(-8.66, -0.71) * mm, v(-8.03, -1.26) * mm, v(-4.48, -4) * mm, v(-0.33, -6.16) * mm, v(8.02, -6.15) * mm, v(12.22, -4) * mm, v(15.77, -1.25) * mm, v(16.4, -0.7) * mm, v(17.18, 0.09) * mm, v(17.41, 0.34) * mm, v(17.83, 0.83) * mm, v(18.02, 1.07) * mm, v(18.85, 2.23) * mm, v(19.22, 3.07) * mm, v(19.58, 3.93) * mm]});
            skFitSpline(sketch, "E76", {"points": [v(-11.84, 4.52) * mm, v(-11.61, 3.26) * mm], "startDerivative": vector(0.12, -1.5) * mm, "endDerivative": vector(0.38, -0.94) * mm});
            skFitSpline(sketch, "E77", {"points": [v(19.3, 3.27) * mm, v(19.56, 4.52) * mm], "startDerivative": vector(0.45, 1.16) * mm, "endDerivative": vector(0.05, 1.26) * mm});
            skSolve(sketch);
        }
        {
            var Q0;
            Q0=qCreatedBy(makeId("Top.planeOp"),FACE);
            var sketch = newSketch(context, id + "F64", { "sketchPlane" : qUnion([Q0])});
            skPoint(sketch, "E78.0", {"position": v(-3.86, 9.65) * mm});
            skLineSegment(sketch, "E79", {"start": v(-3.86, 9.65) * mm, "end": v(-3.86, 37.37) * mm});
            skSolve(sketch);
        }
        {
            var Q0;
            Q0 = qSketchRegion(id + "F63", true);
            var Q1;
            Q1 = qSketchRegion(id + "F55", true);
            var Q2;
            Q2 = qSketchRegion(id + "F56", true);
            var Q3;
            Q3 = qSketchRegion(id + "F57", true);
            var Q4;
            Q4 = qConstructionFilter(qBodyType(qCreatedBy(id + "F64" ,EDGE), BodyType.WIRE), ConstructionObject.NO);
            sweep(context, id + "F65", {"operationType" : NewBodyOperationType.ADD, "profiles" : qUnion([Q0, Q1, Q2, Q3]), "path" : qUnion([Q4])});
        }
        {
            var Q0;
            Q0=qCreatedBy(makeId("Top.planeOp"),FACE);
            cPlane(context, id + "F66", {"entities" : qUnion([Q0]), "cplaneType" : CPlaneType.OFFSET, "offset" : 10.67 * mm, "width" : 152.4 * mm, "height" : 152.4 * mm});
        }
        {
            var Q0;
            Q0=qCreatedBy(id+"F66.planeOp",FACE);
            var sketch = newSketch(context, id + "F67", { "sketchPlane" : qUnion([Q0])});
            skPoint(sketch, "E80.0", {"position": v(-3.86, 22.1) * mm});
            skPoint(sketch, "E81.0", {"position": v(-3.86, 37.37) * mm});
            skLineSegment(sketch, "E82", {"start": v(-10.2, 22.1) * mm, "end": v(-10.2, 37.37) * mm});
            skLineSegment(sketch, "E83", {"start": v(-3.86, 15.78) * mm, "end": v(-3.86, 37.37) * mm});
            skFitSpline(sketch, "E84", {"points": [v(-10.2, 22.1) * mm, v(-3.86, 15.78) * mm], "startDerivative": vector(-0.62, -11.45) * mm, "endDerivative": vector(10.98, 0) * mm});
            skLineSegment(sketch, "E85", {"start": v(-10.2, 37.37) * mm, "end": v(-3.86, 37.37) * mm});
            skSolve(sketch);
        }
        {
            var Q0;
            Q0 = qSketchRegion(id + "F67", true);
            var Q1;
            Q1=sQuery(id+"F67.wireOp",EDGE,"E83");
            revolve(context, id + "F68", {"surfaceOperationType" : NewSurfaceOperationType.NEW, "entities" : qUnion([Q0]), "axis" : qUnion([Q1]), "revolveType" : RevolveType.FULL});
        }
        {
            var Q0;
            Q0=qCreatedBy(id+"F60.planeOp",FACE);
            var sketch = newSketch(context, id + "F69", { "sketchPlane" : qUnion([Q0])});
            skFitSpline(sketch, "E86", {"points": [v(37.37, 17.02) * mm, v(43.51, 17.5) * mm, v(52.08, 16.16) * mm, v(60.7, 12.75) * mm, v(64.52, 10.72) * mm], "startDerivative": vector(25.5, 3.45) * mm, "endDerivative": vector(17, -10.73) * mm});
            skFitSpline(sketch, "E87", {"points": [v(131.8, 10.72) * mm, v(105, 7.93) * mm, v(81.26, 6.52) * mm, v(61.5, -0.8) * mm, v(52.13, -6.05) * mm, v(37.37, -8.3) * mm], "startDerivative": vector(-87.73, -5.7) * mm, "endDerivative": vector(-88.4, -0.16) * mm});
            skLineSegment(sketch, "E88", {"start": v(64.52, 10.72) * mm, "end": v(64.52, 0.8) * mm});
            skLineSegment(sketch, "E89", {"start": v(37.37, 17.02) * mm, "end": v(37.37, -8.3) * mm});
            skSolve(sketch);
        }
        {
            var Q0;
            Q0 = qSketchRegion(id + "F69", true);
            extrude(context, id + "F70", {"entities" : qUnion([Q0]), "endBound" : BoundingType.SYMMETRIC, "depth" : 31.5 * mm, "offsetDistance" : 25.4 * mm});
        }
        {
            var Q0;
            Q0=makeQuery(id+"F70.opExtrude","SWEPT_FACE",FACE,{"disambiguationData":[OSD([sQuery(id+"F69.wireOp",EDGE,"E88")])]});
            var sketch = newSketch(context, id + "F71", { "sketchPlane" : qUnion([Q0])});
            skFitSpline(sketch, "E90", {"points": [v(3.82, 17.19) * mm, v(-1.34, 16.36) * mm, v(-7.17, 9.15) * mm, v(-7.6, 8.65) * mm, v(-8.32, 8.32) * mm, v(-9.34, 7.65) * mm, v(-10.66, 6.38) * mm, v(-11.19, 5.65) * mm, v(-11.72, 4.64) * mm, v(-11.9, 3.86) * mm], "startDerivative": vector(4.57, 0) * mm, "endDerivative": vector(-1.45, -10.4) * mm});
            skLineSegment(sketch, "E91.0", {"start": v(3.86, 7) * mm, "end": v(3.86, 2.15) * mm});
            skFitSpline(sketch, "E92.MirrorCS", {"points": [v(3.89, 17.19) * mm, v(9.05, 16.36) * mm, v(14.88, 9.15) * mm, v(15.31, 8.65) * mm, v(16.03, 8.32) * mm, v(17.06, 7.65) * mm, v(18.38, 6.38) * mm, v(18.9, 5.65) * mm, v(19.43, 4.64) * mm, v(19.6, 3.86) * mm], "startDerivative": vector(-4.57, 0) * mm, "endDerivative": vector(1.45, -10.4) * mm});
            skLineSegment(sketch, "E93", {"start": v(-11.9, 3.86) * mm, "end": v(-17, 22.35) * mm});
            skLineSegment(sketch, "E94", {"start": v(-17, 22.35) * mm, "end": v(23.5, 22.35) * mm});
            skLineSegment(sketch, "E95", {"start": v(23.5, 22.35) * mm, "end": v(19.6, 3.86) * mm});
            skLineSegment(sketch, "E96", {"start": v(3.89, 17.19) * mm, "end": v(3.82, 17.19) * mm});
            skSolve(sketch);
        }
        {
            var Q0;
            Q0 = qSketchRegion(id + "F71", true);
            extrude(context, id + "F72", {"entities" : qUnion([Q0]), "operationType" : NewBodyOperationType.REMOVE, "oppositeDirection" : true, "depth" : 27.18 * mm, "offsetDistance" : 25.4 * mm});
        }
    });
